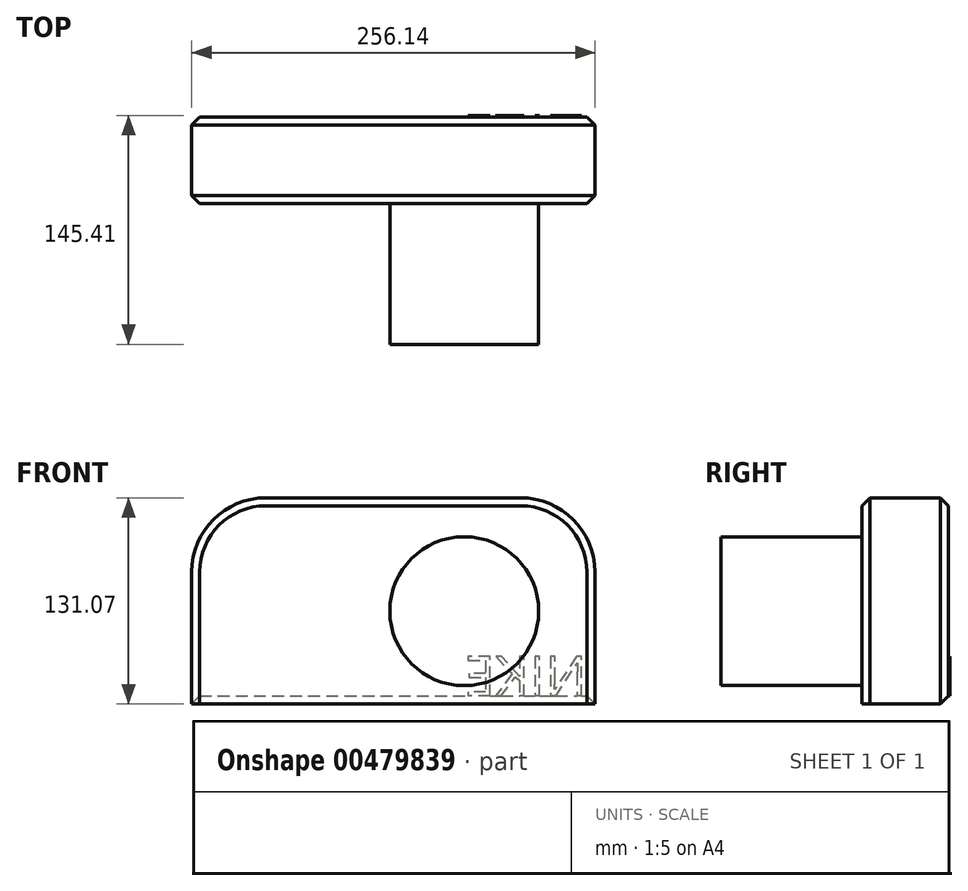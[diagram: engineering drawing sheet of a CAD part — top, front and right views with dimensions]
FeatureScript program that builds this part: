
annotation { "Feature Type Name" : "Feature", "Feature Type Description" : "" }
export const myFeature = defineFeature(function(context is Context, id is Id, definition is map)
    precondition{}
    {
        {
            var Q0;
            Q0=qCreatedBy(makeId("Front.planeOp"),FACE);
            var sketch = newSketch(context, id + "F0", { "sketchPlane" : qUnion([Q0])});
            skLineSegment(sketch, "E0.bottom", {"start": v(-93.93, 70.95) * mm, "end": v(162.2, 70.95) * mm});
            skLineSegment(sketch, "E0.top", {"start": v(-93.93, -60.12) * mm, "end": v(162.2, -60.12) * mm});
            skLineSegment(sketch, "E0.left", {"start": v(-93.93, 70.95) * mm, "end": v(-93.93, -60.12) * mm});
            skLineSegment(sketch, "E0.right", {"start": v(162.2, 70.95) * mm, "end": v(162.2, -60.12) * mm});
            skSolve(sketch);
        }
        {
            var Q0;
            Q0 = qSketchRegion(id + "F0", true);
            extrude(context, id + "F1", {"entities" : qUnion([Q0]), "depth" : 54.86 * mm});
        }
        {
            var Q0;
            Q0=makeQuery(id+"F1.opExtrude","SWEPT_EDGE",EDGE,{"disambiguationData":[OSD([sQuery(id+"F0.wireOp",EDGE,"E0.bottom"),sQuery(id+"F0.wireOp",EDGE,"E0.right")])]});
            var Q1;
            Q1=makeQuery(id+"F1.opExtrude","SWEPT_EDGE",EDGE,{"disambiguationData":[OSD([sQuery(id+"F0.wireOp",EDGE,"E0.bottom"),sQuery(id+"F0.wireOp",EDGE,"E0.left")])]});
            fillet(context, id + "F2", {"entities" : qUnion([Q0, Q1]), "radius" : 47.22 * mm, "tangentPropagation" : true, "allowEdgeOverflow" : false});
        }
        {
            var Q0;
            {var subQ0=sQuery(id+"F0.wireOp",EDGE,"E0.right");var subQ1=sQuery(id+"F0.wireOp",EDGE,"E0.bottom");Q0=makeQuery(id+"F2.opFillet","BLEND_EDGE",EDGE,{"blendedFrom":[makeQuery(id+"F1.opExtrude","SWEPT_EDGE",EDGE,{"disambiguationData":[OSD([subQ1,subQ0])]}),makeQuery(id+"F1.opExtrude","CAP_FACE",FACE,{"disambiguationData":[OSD([subQ1,sQuery(id+"F0.wireOp",EDGE,"E0.top"),sQuery(id+"F0.wireOp",EDGE,"E0.left"),subQ0])],"isStart":false})],"blendedInto":[makeQuery(id+"F1.opExtrude","CAP_FACE",FACE,{"disambiguationData":[OSD([subQ1,sQuery(id+"F0.wireOp",EDGE,"E0.top"),sQuery(id+"F0.wireOp",EDGE,"E0.left"),subQ0])],"isStart":false})]});}
            chamfer(context, id + "F3", {"entities" : qUnion([Q0]), "width" : 5.08 * mm, "tangentPropagation" : true});
        }
        {
            var Q0;
            Q0=makeQuery(id+"F1.opExtrude","CAP_FACE",FACE,{"disambiguationData":[OSD([sQuery(id+"F0.wireOp",EDGE,"E0.bottom"),sQuery(id+"F0.wireOp",EDGE,"E0.top"),sQuery(id+"F0.wireOp",EDGE,"E0.left"),sQuery(id+"F0.wireOp",EDGE,"E0.right")])],"isStart":true});
            chamfer(context, id + "F4", {"entities" : qUnion([Q0]), "width" : 5.08 * mm, "tangentPropagation" : true});
        }
        {
            var Q0;
            Q0=makeQuery(id+"F1.opExtrude","CAP_FACE",FACE,{"disambiguationData":[OSD([sQuery(id+"F0.wireOp",EDGE,"E0.bottom"),sQuery(id+"F0.wireOp",EDGE,"E0.top"),sQuery(id+"F0.wireOp",EDGE,"E0.left"),sQuery(id+"F0.wireOp",EDGE,"E0.right")])],"isStart":false});
            var sketch = newSketch(context, id + "F5", { "sketchPlane" : qUnion([Q0])});
            skCircle(sketch, "E1", {"center": v(79.22, -1.07) * mm, "radius": 47.28 * mm});
            skSolve(sketch);
        }
        {
            var Q0;
            Q0 = qSketchRegion(id + "F5", true);
            extrude(context, id + "F6", {"entities" : qUnion([Q0]), "operationType" : NewBodyOperationType.ADD, "depth" : 25.4 * mm});
        }
        {
            var Q0;
            Q0=makeQuery(id+"F1.opExtrude","CAP_FACE",FACE,{"disambiguationData":[OSD([sQuery(id+"F0.wireOp",EDGE,"E0.bottom"),sQuery(id+"F0.wireOp",EDGE,"E0.top"),sQuery(id+"F0.wireOp",EDGE,"E0.left"),sQuery(id+"F0.wireOp",EDGE,"E0.right")])],"isStart":true});
            var sketch = newSketch(context, id + "F7", { "sketchPlane" : qUnion([Q0])});
            skText(sketch, "E2", { "text": "NIKE", "fontName": "OpenSans-Regular.ttf"});
            const initialGuessF7  = {"E2": [-0.15713, -0.05504, 1, 0, 0.02536]};
            skSetInitialGuess(sketch, initialGuessF7);
            skSolve(sketch);
        }
        {
            var Q0;
            Q0 = qSketchRegion(id + "F7", true);
            extrude(context, id + "F8", {"entities" : qUnion([Q0]), "operationType" : NewBodyOperationType.ADD, "depth" : 1.02 * mm});
        }
        {
            var Q0;
            Q0=makeQuery(id+"F6.opExtrude","CAP_FACE",FACE,{"disambiguationData":[OSD([sQuery(id+"F5.wireOp",EDGE,"E1")])],"isStart":false});
            extrude(context, id + "F9", {"entities" : qUnion([Q0]), "operationType" : NewBodyOperationType.ADD, "depth" : 24.13 * mm});
        }
        {
            var Q0;
            Q0=makeQuery(id+"F9.opExtrude","CAP_FACE",FACE,{"disambiguationData":[OSD([sQuery(id+"F5.wireOp",EDGE,"E1")])],"isStart":false});
            extrude(context, id + "F10", {"entities" : qUnion([Q0]), "operationType" : NewBodyOperationType.ADD, "depth" : 40 * mm});
        }
    });
